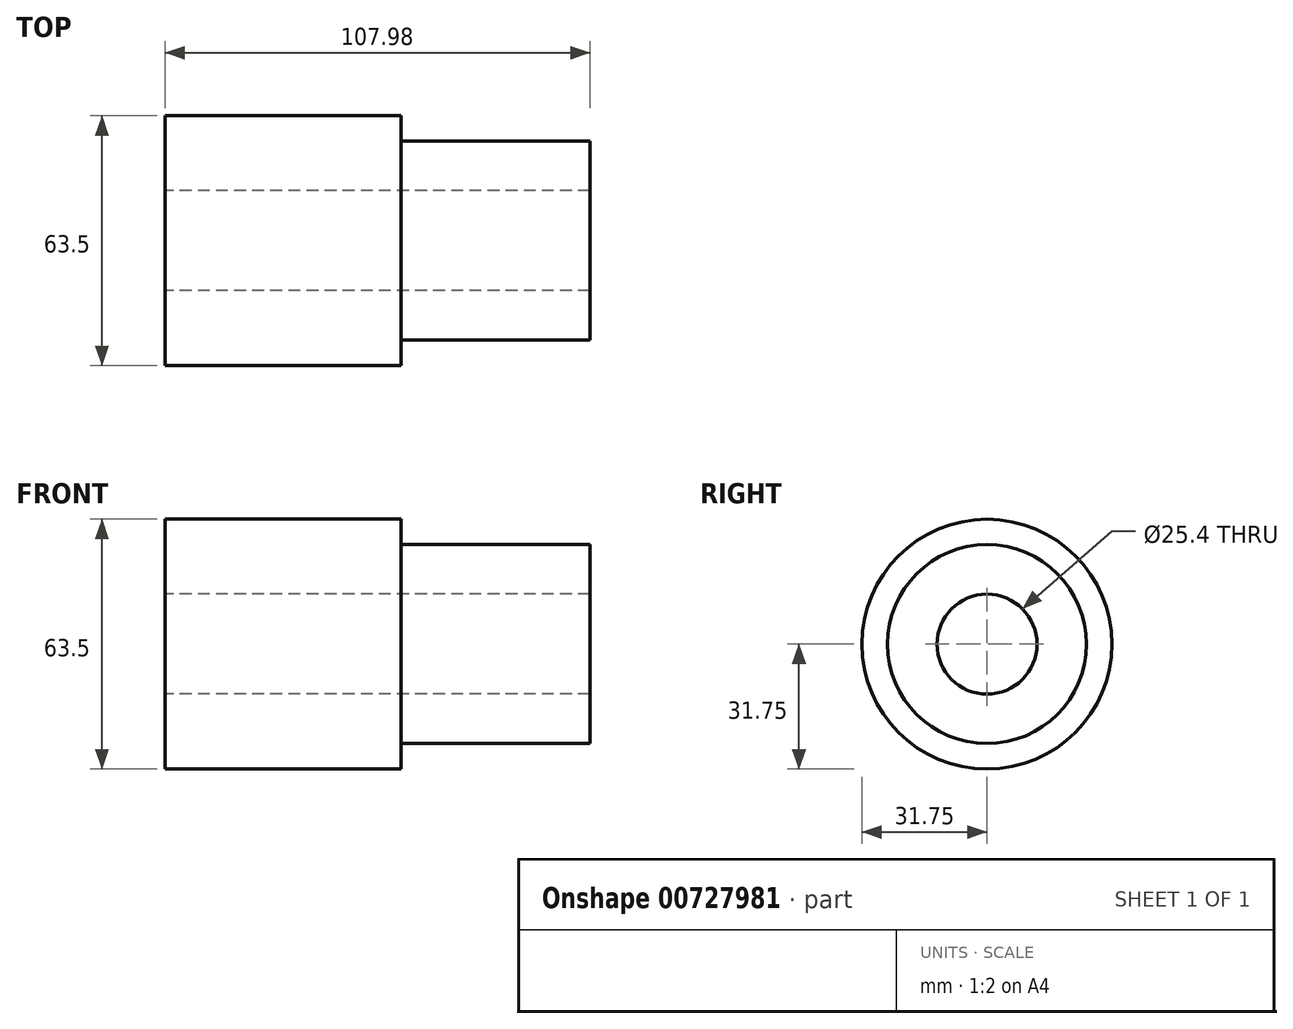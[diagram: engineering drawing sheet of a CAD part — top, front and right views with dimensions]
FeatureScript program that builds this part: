
annotation { "Feature Type Name" : "Feature", "Feature Type Description" : "" }
export const myFeature = defineFeature(function(context is Context, id is Id, definition is map)
    precondition{}
    {
        {
            var Q0;
            Q0=qCreatedBy(makeId("Right.planeOp"),FACE);
            var sketch = newSketch(context, id + "F0", { "sketchPlane" : qUnion([Q0])});
            skCircle(sketch, "E0", {"center": v(0, 0) * mm, "radius": 31.75 * mm});
            skCircle(sketch, "E1", {"center": v(0, 0) * mm, "radius": 19.05 * mm});
            skSolve(sketch);
        }
        {
            var Q0;
            Q0=makeQuery(id+"F0.imprint","IMPRINT",FACE,{"disambiguationData":[TD([[makeQuery(id+"F0.imprint","IMPRINT",EDGE,{"derivedFrom":sQuery(id+"F0.wireOp",EDGE,"E0")}),1.0]])]});
            var Q1;
            Q1 = qSketchRegion(id + "F2", true);
            extrude(context, id + "F1", {"entities" : qUnion([Q0, Q1]), "depth" : 59.94 * mm, "offsetDistance" : 25.4 * mm});
        }
        {
            var Q0;
            Q0=qCreatedBy(makeId("Right.planeOp"),FACE);
            var sketch = newSketch(context, id + "F2", { "sketchPlane" : qUnion([Q0])});
            skCircle(sketch, "E2", {"center": v(0, 0) * mm, "radius": 25.27 * mm});
            skSolve(sketch);
        }
        {
            var Q0;
            Q0=qCreatedBy(makeId("Right.planeOp"),FACE);
            var sketch = newSketch(context, id + "F3", { "sketchPlane" : qUnion([Q0])});
            skCircle(sketch, "E3", {"center": v(0, 0) * mm, "radius": 12.7 * mm});
            skSolve(sketch);
        }
        {
            var Q0;
            Q0 = qSketchRegion(id + "F2", true);
            extrude(context, id + "F4", {"entities" : qUnion([Q0]), "operationType" : NewBodyOperationType.ADD, "endBound" : BoundingType.THROUGH_ALL, "depth" : 50.8 * mm, "offsetDistance" : 25.4 * mm});
        }
        {
            var Q0;
            Q0 = qSketchRegion(id + "F3", true);
            extrude(context, id + "F5", {"entities" : qUnion([Q0]), "operationType" : NewBodyOperationType.REMOVE, "endBound" : BoundingType.THROUGH_ALL, "depth" : 76.2 * mm, "offsetDistance" : 25.4 * mm});
        }
    });
